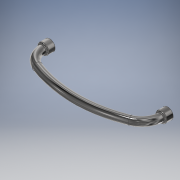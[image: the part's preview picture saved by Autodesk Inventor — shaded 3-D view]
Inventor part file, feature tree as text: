
AUTODESK INVENTOR PART (.ipt)
format: ipt  version: 2019 (Build 230136000, 136)  size: 182,784 bytes
history: native  units: mm
features: sketch x2, other x1, sweep x1, extrude x1, mirror x1, fillet x1
ambient origin geometry x8: Origin, YZ Plane, XZ Plane, XY Plane, X Axis, Y Axis, Z Axis, Center Point
bodies: Body1 (feature_tree)
feature tree (7):
  other  "Твердое тело1"
  sketch  "Эскиз1"
  sketch  "Эскиз2"
  sweep  "Сдвиг1"
  extrude  "Выдавливание1"  Depth=25.0mm
  mirror  "Зеркальное отражение1"
  fillet  "Сопряжение1"  Radius=10.0mm
